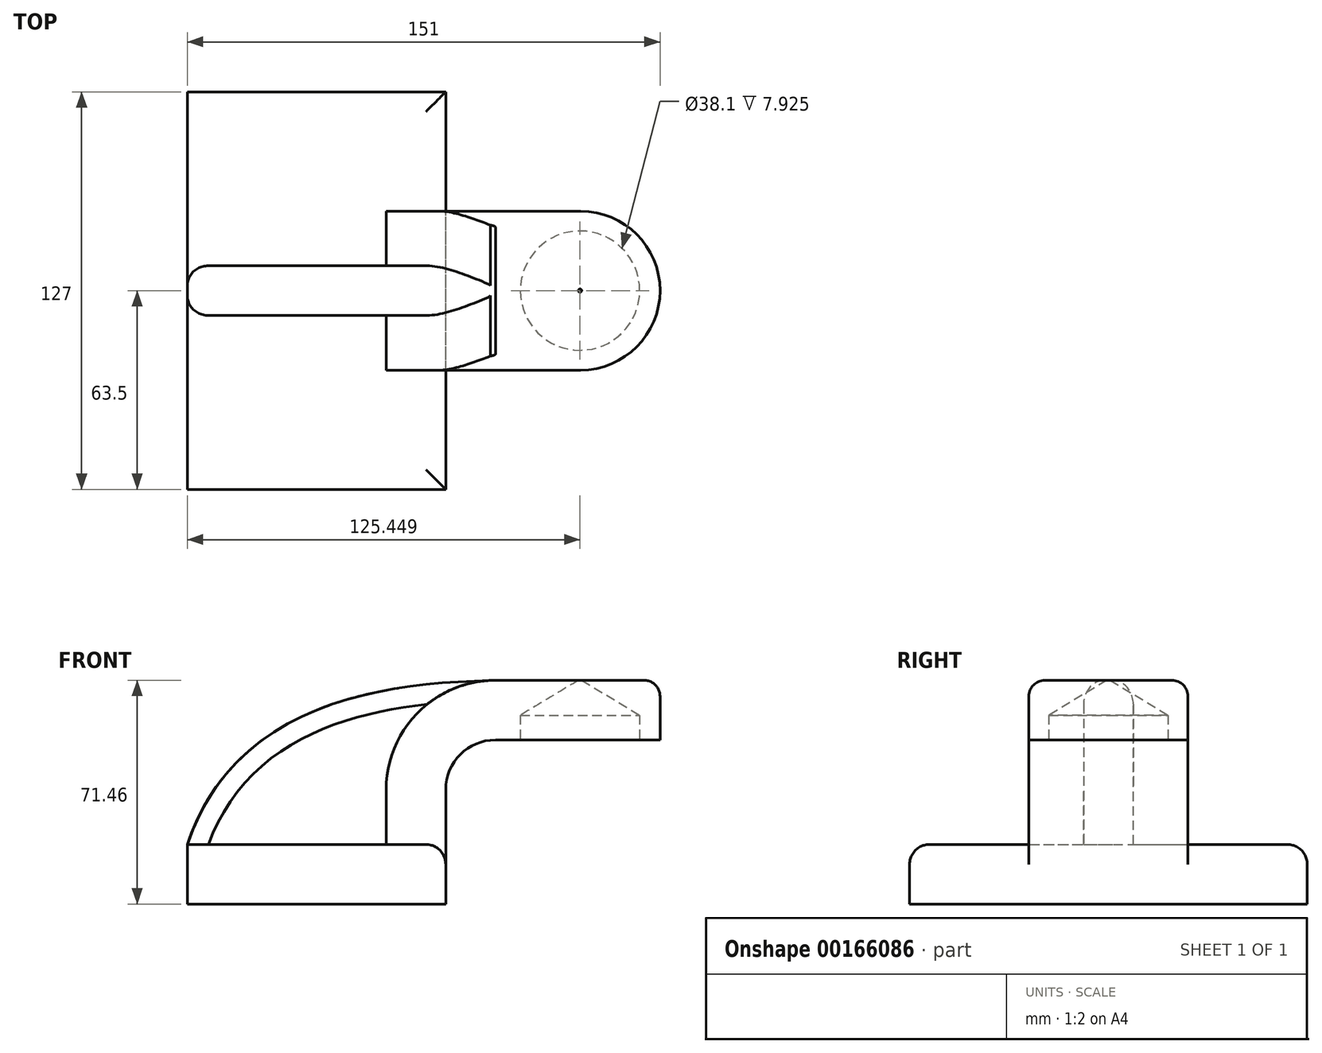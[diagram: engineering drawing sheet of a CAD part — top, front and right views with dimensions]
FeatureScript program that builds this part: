
annotation { "Feature Type Name" : "Feature", "Feature Type Description" : "" }
export const myFeature = defineFeature(function(context is Context, id is Id, definition is map)
    precondition{}
    {
        {
            var Q0;
            Q0=qCreatedBy(makeId("Front.planeOp"),FACE);
            var sketch = newSketch(context, id + "F0", { "sketchPlane" : qUnion([Q0])});
            skLineSegment(sketch, "E0.bottom", {"start": v(-41.28, 9.52) * mm, "end": v(41.27, 9.53) * mm});
            skLineSegment(sketch, "E0.top", {"start": v(-41.28, -9.53) * mm, "end": v(41.28, -9.53) * mm});
            skLineSegment(sketch, "E0.left", {"start": v(-41.28, 9.52) * mm, "end": v(-41.27, -9.53) * mm});
            skLineSegment(sketch, "E0.right", {"start": v(41.28, 9.53) * mm, "end": v(41.28, -9.52) * mm});
            skPoint(sketch, "E0.middle", {"position": v(0, 0) * mm});
            skLineSegment(sketch, "E1.bottom", {"start": v(58.92, 38.1) * mm, "end": v(109.72, 38.1) * mm});
            skLineSegment(sketch, "E1.top", {"start": v(58.92, 66.67) * mm, "end": v(109.72, 66.67) * mm});
            skLineSegment(sketch, "E1.left", {"start": v(58.92, 38.1) * mm, "end": v(58.92, 66.68) * mm});
            skLineSegment(sketch, "E1.right", {"start": v(109.72, 38.1) * mm, "end": v(109.72, 66.68) * mm});
            skPoint(sketch, "E1.middle", {"position": v(84.32, 52.39) * mm});
            skLineSegment(sketch, "E2", {"start": v(41.27, 9.53) * mm, "end": v(41.27, 27) * mm});
            skArc(sketch, "E3", {"start": v(41.27, 27) * mm, "mid": v(45.92, 38.23) * mm, "end": v(57.15, 42.88) * mm});
            skLineSegment(sketch, "E4", {"start": v(57.15, 42.88) * mm, "end": v(78.48, 42.88) * mm});
            skLineSegment(sketch, "E5.0", {"start": v(57.15, 61.93) * mm, "end": v(78.48, 61.93) * mm});
            skArc(sketch, "E5.1", {"start": v(22.23, 27) * mm, "mid": v(32.45, 51.7) * mm, "end": v(57.15, 61.93) * mm});
            skLineSegment(sketch, "E5.2", {"start": v(22.23, 9.53) * mm, "end": v(22.23, 27) * mm});
            skFitSpline(sketch, "E6", {"points": [v(-41.28, 9.53) * mm, v(57.15, 61.93) * mm], "startDerivative": vector(47.1, 138.63) * mm, "endDerivative": vector(103.02, 2.13) * mm});
            skLineSegment(sketch, "E7", {"start": v(78.48, 61.93) * mm, "end": v(84.32, 61.93) * mm});
            skLineSegment(sketch, "E8", {"start": v(78.48, 42.88) * mm, "end": v(84.32, 42.88) * mm});
            skLineSegment(sketch, "E9", {"start": v(84.32, 61.93) * mm, "end": v(109.72, 61.93) * mm});
            skLineSegment(sketch, "E10", {"start": v(84.32, 42.88) * mm, "end": v(109.72, 42.88) * mm});
            skLineSegment(sketch, "E11", {"start": v(84.32, 42.88) * mm, "end": v(84.32, 61.93) * mm});
            skLineSegment(sketch, "E12", {"start": v(84.32, 61.93) * mm, "end": v(84.32, 66.67) * mm});
            skLineSegment(sketch, "E13", {"start": v(84.32, 66.67) * mm, "end": v(84.32, 38.1) * mm});
            skSolve(sketch);
        }
        {
            var Q0;
            Q0=makeQuery(id+"F0.imprint","IMPRINT",FACE,{"disambiguationData":[TD([[makeQuery(id+"F0.imprint","IMPRINT",EDGE,{"derivedFrom":sQuery(id+"F0.wireOp",EDGE,"E0.top")}),1.0]])]});
            extrude(context, id + "F1", {"entities" : qUnion([Q0]), "endBound" : BoundingType.SYMMETRIC, "depth" : 127 * mm});
        }
        {
            var Q0;
            {var subQ1=sQuery(id+"F0.wireOp",EDGE,"E2");Q0=makeQuery(id+"F0.imprint","IMPRINT",FACE,{"disambiguationData":[TD([[makeQuery(id+"F0.imprint","IMPRINT",EDGE,{"derivedFrom":subQ1}),1.0]])]});}
            var Q1;
            {var subQ0=sQuery(id+"F0.wireOp",EDGE,"E7");Q1=makeQuery(id+"F0.imprint","IMPRINT",FACE,{"disambiguationData":[TD([[makeQuery(id+"F0.imprint","IMPRINT",EDGE,{"derivedFrom":subQ0}),-1.0]])]});}
            extrude(context, id + "F2", {"entities" : qUnion([Q0, Q1]), "operationType" : NewBodyOperationType.ADD, "endBound" : BoundingType.SYMMETRIC, "depth" : 50.8 * mm});
        }
        {
            var Q0;
            {var subQ3=sQuery(id+"F0.wireOp",EDGE,"E5.2");Q0=makeQuery(id+"F0.imprint","IMPRINT",FACE,{"disambiguationData":[TD([[makeQuery(id+"F0.imprint","IMPRINT",EDGE,{"derivedFrom":subQ3}),1.0]])]});}
            extrude(context, id + "F3", {"entities" : qUnion([Q0]), "operationType" : NewBodyOperationType.ADD, "endBound" : BoundingType.SYMMETRIC, "depth" : 15.88 * mm});
        }
        {
            var Q0;
            Q0=makeQuery(id+"F1.opExtrude","CAP_EDGE",EDGE,{"disambiguationData":[OSD([sQuery(id+"F0.wireOp",EDGE,"E0.bottom")])],"isStart":false});
            var Q1;
            {var subQ0=sQuery(id+"F0.wireOp",EDGE,"E2");var subQ1=sQuery(id+"F0.wireOp",EDGE,"E0.bottom");var subQ2=sQuery(id+"F0.wireOp",EDGE,"E0.right");Q1=makeQuery(id+"F2.boolean.opBoolean","SPLIT",EDGE,{"disambiguationData":[TD([makeQuery(id+"F1.opExtrude","CAP_FACE",FACE,{"disambiguationData":[OSD([subQ1,sQuery(id+"F0.wireOp",EDGE,"E0.top"),sQuery(id+"F0.wireOp",EDGE,"E0.left"),subQ2])],"isStart":false})])],"derivedFrom":makeQuery(id+"F1.opExtrude","SWEPT_EDGE",EDGE,{"disambiguationData":[OSD([subQ1,subQ2,subQ0])]})});}
            var Q2;
            Q2=makeQuery(id+"F1.opExtrude","CAP_EDGE",EDGE,{"disambiguationData":[OSD([sQuery(id+"F0.wireOp",EDGE,"E0.bottom")])],"isStart":true});
            var Q3;
            {var subQ0=sQuery(id+"F0.wireOp",EDGE,"E2");var subQ1=sQuery(id+"F0.wireOp",EDGE,"E0.bottom");var subQ2=sQuery(id+"F0.wireOp",EDGE,"E0.right");Q3=makeQuery(id+"F2.boolean.opBoolean","SPLIT",EDGE,{"disambiguationData":[TD([makeQuery(id+"F1.opExtrude","CAP_FACE",FACE,{"disambiguationData":[OSD([subQ1,sQuery(id+"F0.wireOp",EDGE,"E0.top"),sQuery(id+"F0.wireOp",EDGE,"E0.left"),subQ2])],"isStart":true})])],"derivedFrom":makeQuery(id+"F1.opExtrude","SWEPT_EDGE",EDGE,{"disambiguationData":[OSD([subQ1,subQ2,subQ0])]})});}
            var Q4;
            Q4=makeQuery(id+"F3.opExtrude","CAP_EDGE",EDGE,{"disambiguationData":[OSD([sQuery(id+"F0.wireOp",EDGE,"E6")])],"isStart":true});
            var Q5;
            Q5=makeQuery(id+"F3.opExtrude","CAP_EDGE",EDGE,{"disambiguationData":[OSD([sQuery(id+"F0.wireOp",EDGE,"E6")])],"isStart":false});
            fillet(context, id + "F4", {"entities" : qUnion([Q0, Q1, Q2, Q3, Q4, Q5]), "radius" : 6.35 * mm, "tangentPropagation" : true, "allowEdgeOverflow" : false});
        }
        {
            var Q0;
            {var subQ0=sQuery(id+"F0.wireOp",EDGE,"E9");Q0=makeQuery(id+"F0.imprint","IMPRINT",FACE,{"disambiguationData":[TD([[makeQuery(id+"F0.imprint","IMPRINT",EDGE,{"derivedFrom":subQ0}),-1.0]])]});}
            var Q1;
            Q1=sQuery(id+"F0.wireOp",EDGE,"E11");
            revolve(context, id + "F5", {"operationType" : NewBodyOperationType.ADD, "entities" : qUnion([Q0]), "axis" : qUnion([Q1]), "revolveType" : RevolveType.FULL});
        }
        {
            var Q0;
            Q0=makeQuery(id+"F5.opRevolve","SWEPT_EDGE",EDGE,{"disambiguationData":[OSD([sQuery(id+"F0.wireOp",EDGE,"E1.right"),sQuery(id+"F0.wireOp",EDGE,"E9")])]});
            var Q1;
            Q1=makeQuery(id+"F2.opExtrude","CAP_EDGE",EDGE,{"disambiguationData":[OSD([sQuery(id+"F0.wireOp",EDGE,"E5.0"),sQuery(id+"F0.wireOp",EDGE,"E7")])],"isStart":true});
            var Q2;
            Q2=makeQuery(id+"F2.opExtrude","CAP_EDGE",EDGE,{"disambiguationData":[OSD([sQuery(id+"F0.wireOp",EDGE,"E5.0"),sQuery(id+"F0.wireOp",EDGE,"E7")])],"isStart":false});
            fillet(context, id + "F6", {"entities" : qUnion([Q0, Q1, Q2]), "radius" : 5.08 * mm, "tangentPropagation" : true, "allowEdgeOverflow" : false});
        }
        {
            var Q0;
            Q0=qCreatedBy(makeId("Top.planeOp"),FACE);
            var sketch = newSketch(context, id + "F7", { "sketchPlane" : qUnion([Q0])});
            skCircle(sketch, "E14", {"center": v(84.17, 0) * mm, "radius": 17.6 * mm});
            skSolve(sketch);
        }
        {
            var Q0;
            Q0=sQuery(id+"F7.wireOp",VERTEX,"E14.center");
            var Q1;
            Q1=makeQuery(id+"F1.opExtrude","SWEPT_BODY",BODY,{"disambiguationData":[OSD([sQuery(id+"F0.wireOp",EDGE,"E0.bottom"),sQuery(id+"F0.wireOp",EDGE,"E0.top"),sQuery(id+"F0.wireOp",EDGE,"E0.left"),sQuery(id+"F0.wireOp",EDGE,"E0.right")])]});
            hole(context, id + "F8", {"style" : HoleStyle.SIMPLE, "endStyle" : HoleEndStyle.BLIND, "oppositeDirection" : true, "holeDiameter" : 38.1 * mm, "holeDepth" : 50.8 * mm, "startFromSketch" : true, "locations" : qUnion([Q0]), "scope" : qUnion([Q1])});
        }
    });
